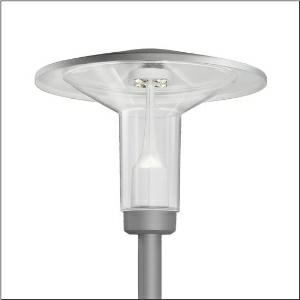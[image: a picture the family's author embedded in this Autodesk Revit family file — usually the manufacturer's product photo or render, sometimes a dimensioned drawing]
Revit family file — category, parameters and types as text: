
# Revit family: laterne_iq___st1_2a_5xa5255kf14hp_e09e
name_source: partatom
category: Lighting Fixtures
units: mm (PartAtom-declared; Revit-internal decimal feet)

## family parameters
Cut with Voids When Loaded = No
Host = Face
Light Source = No
Part Type = Normal
Room Calculation Point = No
Round Connector Dimension = Use Diameter
Shared = No

## types (1)
- --- (1 x LED, 4940 lm, 33.6 W, 4000K)
    Apparent Load = 34 VA
    CIE Flux Codes = 25 63 94 98 100
    Color Rendering = 70
    Color Temperature = 4000K
    Default Elevation = 1800 mm
    Description = Lantern iQ, mast luminaire, Module 540 iQ-SR, primary light control with 3 zone facetted reflector, of plastic, silver coated, highly specular, structured, primary optical cover: cover, of PMMA, transparent, light distribution: ST1.2a, light emission: direct distribution, primary light characteristic: asymmetric, installation type: post-top, LED, High Power LED, rated luminous flux: 4.940lm, luminous efficacy: 147lm/W, light colour: 740, colour temperature: 4000K, control gear: iQ Street-Remote, control: pre-setting: logarithmic dimming characteristic, Street-Remote, Auto-Match, Temp-Guard, Lumen-Switch, Night-Set, Smart-Wire, Light-Fading, Desk-Remote (wireless, voltage-free reading and setting of iQ features in the workshop via application-optimized NFC function/RFID function), optimised constant luminous flux control (CLO 2.0), with terminal, 6-pole, max. 2.5mm², mains connection: 230..240V, AC, 50/60Hz, start of lifetime: 34W, end of service life: 36W, reduction: 15W, luminaire housing, upper part, of glass-fibre reinforced polyester, coated, Siteco® metallic grey (DB 702S), diameter: 750mm, height: 583mm, spigot size: d x l = 76 x 70mm (post-top) | with reducer (optional accessory) 60 x 70mm, mounting height: 3..5m, post-top mast mounting element, of diecast aluminium, coated, Siteco® metallic grey (DB 702S), Module 540 iQ-SR, traffic white (RAL 9016), equipment: Power, protection rating (complete): IP65, insulation class (complete): insulation class II (safety insulation), certification: CE, ENEC, VDE, packaging unit: 1 piece

Light Distribution: ST1.2a
    Height = 583 mm
    Lamp = 1 x LED
    Lamp Light Flux = 4940 lm
    Lamp Power = 33.6 W
    Lamp count = 1
    Length = 750 mm
    Luminous efficacy = 147 lm/W
    Manufacturer = Siteco
    ModVariant = No
    Model = 5XA5255KF14HP
    Number of Poles = 1
    OnlyDefault = Yes
    Power Factor = 1
    Product Name = Laterne iQ | ST1.2a
    Product group = mast luminaire | pylon top
    ProductGroupID = 6100
    Protection Class = Protection class II
    Protection Degree = IP 65
    RLX_Detail_Level = 1
    RLX_Emergency_Light_Flux = 0 lm
    RLX_Emergency_Type = 0
    RLX_Emergency_Type_DB = No
    RlxData = <blob elided: 34169 chars, md5=24612798>
    Socket = socket
    Standby Power = 0 W
    System Light Flux = 4940 lm
    System Power = 34 W
    Type Comments = factory setting: luminous flux: 100 % | dim-lin: 254 | 695 mA
    Type Image = l_1006050.jpg
    URL = http://relux.com
    VarID = @adj_214769
    Voltage = 0 V
    Weight = 0.00 kg
    Width = 0 mm  [stored 0 ft]

note: [stored X ft] marks values corroborated as IEEE doubles in the binary element streams (Revit-internal decimal feet)

## geometry (parser evidence)
native form markers: Blend x4, Sweep x12
no freeform markers — native parametric forms only
